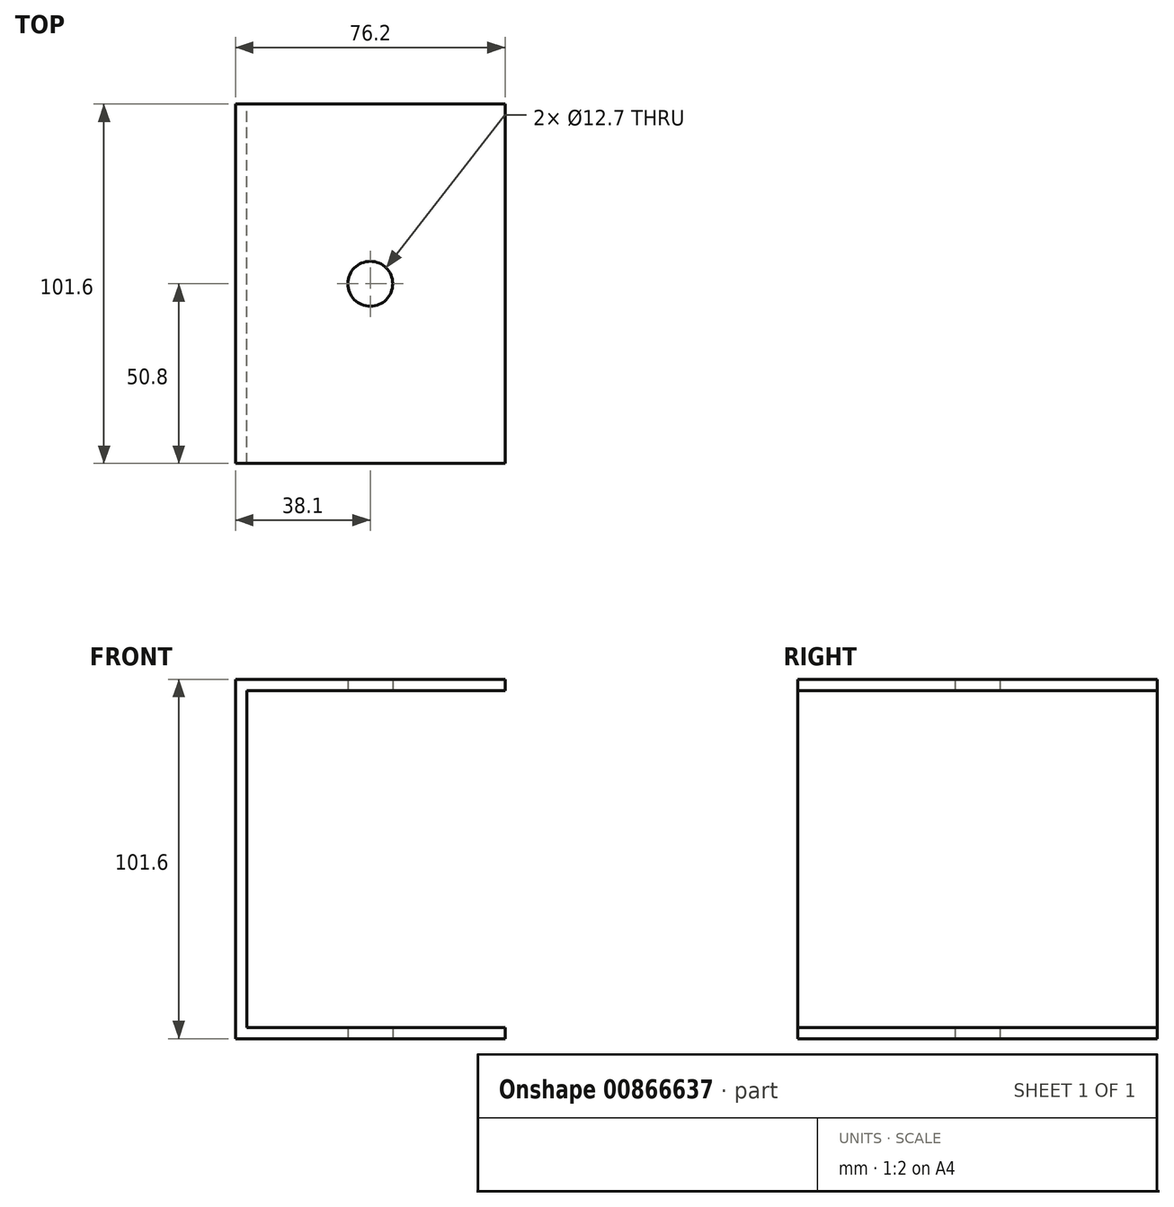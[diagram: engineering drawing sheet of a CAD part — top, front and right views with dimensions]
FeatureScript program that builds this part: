
annotation { "Feature Type Name" : "Feature", "Feature Type Description" : "" }
export const myFeature = defineFeature(function(context is Context, id is Id, definition is map)
    precondition{}
    {
        {
            var Q0;
            Q0=qCreatedBy(makeId("Front.planeOp"),FACE);
            var sketch = newSketch(context, id + "F0", { "sketchPlane" : qUnion([Q0])});
            skLineSegment(sketch, "E0", {"start": v(38.1, 50.8) * mm, "end": v(-38.1, 50.8) * mm});
            skLineSegment(sketch, "E1", {"start": v(-38.1, 50.8) * mm, "end": v(-38.1, -50.8) * mm});
            skLineSegment(sketch, "E2", {"start": v(-38.1, -50.8) * mm, "end": v(38.1, -50.8) * mm});
            skLineSegment(sketch, "E3", {"start": v(38.1, -50.8) * mm, "end": v(38.1, -47.62) * mm});
            skLineSegment(sketch, "E4", {"start": v(38.1, -47.62) * mm, "end": v(-34.92, -47.62) * mm});
            skLineSegment(sketch, "E5", {"start": v(-34.92, -47.62) * mm, "end": v(-34.93, 47.62) * mm});
            skLineSegment(sketch, "E6", {"start": v(-34.92, 47.63) * mm, "end": v(38.1, 47.63) * mm});
            skLineSegment(sketch, "E7", {"start": v(38.1, 47.63) * mm, "end": v(38.1, 50.8) * mm});
            skLineSegment(sketch, "E8", {"start": v(0, 0) * mm, "end": v(-38.1, 0) * mm, "construction": true});
            skLineSegment(sketch, "E9", {"start": v(0, 0) * mm, "end": v(0, 50.8) * mm, "construction": true});
            skSolve(sketch);
        }
        {
            var Q0;
            Q0 = qSketchRegion(id + "F0", true);
            extrude(context, id + "F1", {"entities" : qUnion([Q0]), "endBound" : BoundingType.SYMMETRIC, "depth" : 101.6 * mm, "offsetDistance" : 25.4 * mm});
        }
        {
            var Q0;
            Q0=makeQuery(id+"F1.opExtrude","SWEPT_FACE",FACE,{"disambiguationData":[OSD([sQuery(id+"F0.wireOp",EDGE,"E2")])]});
            var sketch = newSketch(context, id + "F2", { "sketchPlane" : qUnion([Q0])});
            skCircle(sketch, "E10", {"center": v(0, 0) * mm, "radius": 6.35 * mm});
            skSolve(sketch);
        }
        {
            var Q0;
            Q0 = qSketchRegion(id + "F2", true);
            extrude(context, id + "F3", {"entities" : qUnion([Q0]), "operationType" : NewBodyOperationType.REMOVE, "endBound" : BoundingType.THROUGH_ALL, "oppositeDirection" : true, "depth" : 76.2 * mm, "offsetDistance" : 25.4 * mm});
        }
    });
